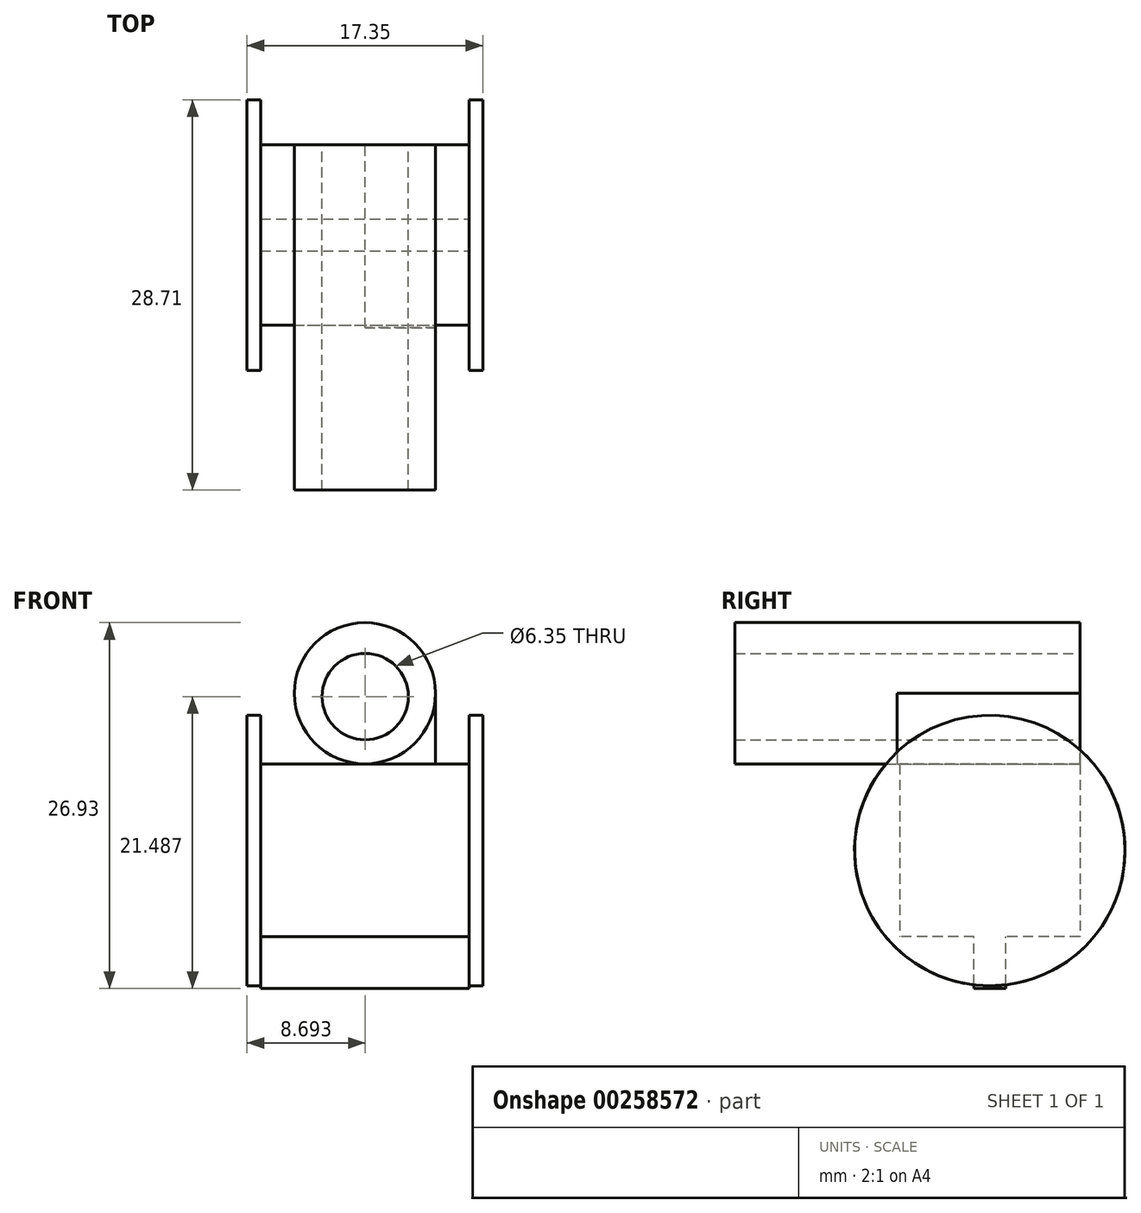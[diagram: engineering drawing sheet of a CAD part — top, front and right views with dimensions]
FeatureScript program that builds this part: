
annotation { "Feature Type Name" : "Feature", "Feature Type Description" : "" }
export const myFeature = defineFeature(function(context is Context, id is Id, definition is map)
    precondition{}
    {
        {
            var Q0;
            Q0=qCreatedBy(makeId("Top.planeOp"),FACE);
            var sketch = newSketch(context, id + "F0", { "sketchPlane" : qUnion([Q0])});
            skLineSegment(sketch, "E0.bottom", {"start": v(-55.18, 45.23) * mm, "end": v(-39.83, 45.23) * mm});
            skLineSegment(sketch, "E0.top", {"start": v(-55.18, 31.95) * mm, "end": v(-39.83, 31.95) * mm});
            skLineSegment(sketch, "E0.left", {"start": v(-55.18, 45.23) * mm, "end": v(-55.18, 31.95) * mm});
            skLineSegment(sketch, "E0.right", {"start": v(-39.83, 45.23) * mm, "end": v(-39.83, 31.95) * mm});
            skSolve(sketch);
        }
        {
            var Q0;
            Q0 = qSketchRegion(id + "F0", true);
            extrude(context, id + "F1", {"entities" : qUnion([Q0]), "depth" : 12.7 * mm});
        }
        {
            var Q0;
            Q0=makeQuery(id+"F1.opExtrude","SWEPT_FACE",FACE,{"disambiguationData":[OSD([sQuery(id+"F0.wireOp",EDGE,"E0.left")])]});
            var sketch = newSketch(context, id + "F2", { "sketchPlane" : qUnion([Q0])});
            skCircle(sketch, "E1", {"center": v(-38.59, 6.35) * mm, "radius": 9.95 * mm});
            skPoint(sketch, "E1.centerSnap0", {"position": v(-31.95, 6.35) * mm});
            skPoint(sketch, "E1.centerSnap1", {"position": v(-38.59, 12.7) * mm});
            skSolve(sketch);
        }
        {
            var Q0;
            Q0=makeQuery(id+"F1.opExtrude","SWEPT_FACE",FACE,{"disambiguationData":[OSD([sQuery(id+"F0.wireOp",EDGE,"E0.right")])]});
            var sketch = newSketch(context, id + "F3", { "sketchPlane" : qUnion([Q0])});
            skCircle(sketch, "E2", {"center": v(38.59, 6.35) * mm, "radius": 9.95 * mm});
            skPoint(sketch, "E2.centerSnap0", {"position": v(38.59, 12.7) * mm});
            skPoint(sketch, "E2.centerSnap1", {"position": v(31.95, 6.35) * mm});
            skSolve(sketch);
        }
        {
            var Q0;
            Q0=makeQuery(id+"F2.imprint","IMPRINT",FACE,{"disambiguationData":[TD([[makeQuery(id+"F2.imprint","IMPRINT",EDGE,{"derivedFrom":sQuery(id+"F2.wireOp",EDGE,"E1")}),1.0]])]});
            var Q1;
            {var subQ0=sQuery(id+"F0.wireOp",EDGE,"E0.left");Q1=makeQuery(id+"F2.imprint","IMPRINT",FACE,{"disambiguationData":[TD([[makeQuery(id+"F2.imprint","IMPRINT",EDGE,{"derivedFrom":makeQuery(id+"F1.opExtrude","CAP_EDGE",EDGE,{"disambiguationData":[OSD([subQ0])],"isStart":true})}),1.0]])]});}
            extrude(context, id + "F4", {"entities" : qUnion([Q0, Q1]), "operationType" : NewBodyOperationType.ADD, "depth" : 1 * mm});
        }
        {
            var Q0;
            Q0=makeQuery(id+"F3.imprint","IMPRINT",FACE,{"disambiguationData":[TD([[makeQuery(id+"F3.imprint","IMPRINT",EDGE,{"derivedFrom":sQuery(id+"F3.wireOp",EDGE,"E2")}),1.0]])]});
            var Q1;
            {var subQ0=sQuery(id+"F0.wireOp",EDGE,"E0.right");Q1=makeQuery(id+"F3.imprint","IMPRINT",FACE,{"disambiguationData":[TD([[makeQuery(id+"F3.imprint","IMPRINT",EDGE,{"derivedFrom":makeQuery(id+"F1.opExtrude","CAP_EDGE",EDGE,{"disambiguationData":[OSD([subQ0])],"isStart":true})}),-1.0]])]});}
            extrude(context, id + "F5", {"entities" : qUnion([Q0, Q1]), "operationType" : NewBodyOperationType.ADD, "depth" : 1 * mm});
        }
        {
            var Q0;
            Q0=makeQuery(id+"F1.opExtrude","SWEPT_FACE",FACE,{"disambiguationData":[OSD([sQuery(id+"F0.wireOp",EDGE,"E0.bottom")])]});
            var sketch = newSketch(context, id + "F6", { "sketchPlane" : qUnion([Q0])});
            skLineSegment(sketch, "E3", {"start": v(47.5, 12.7) * mm, "end": v(47.5, 17.92) * mm});
            skCircle(sketch, "E4", {"center": v(47.5, 17.92) * mm, "radius": 5.2 * mm});
            skLineSegment(sketch, "E5", {"start": v(52.7, 17.92) * mm, "end": v(52.7, 12.7) * mm});
            skLineSegment(sketch, "E6", {"start": v(52.7, 12.7) * mm, "end": v(52.7, 17.92) * mm});
            skLineSegment(sketch, "E7", {"start": v(42.31, 17.92) * mm, "end": v(42.31, 12.7) * mm});
            skSolve(sketch);
        }
        {
            var Q0;
            {var subQ5=sQuery(id+"F6.wireOp",EDGE,"E7");Q0=makeQuery(id+"F6.imprint","IMPRINT",FACE,{"disambiguationData":[TD([[makeQuery(id+"F6.imprint","IMPRINT",EDGE,{"derivedFrom":subQ5}),1.0]])]});}
            var Q1;
            {var subQ5=sQuery(id+"F6.wireOp",EDGE,"E6");Q1=makeQuery(id+"F6.imprint","IMPRINT",FACE,{"disambiguationData":[TD([[makeQuery(id+"F6.imprint","IMPRINT",EDGE,{"derivedFrom":subQ5}),1.0]])]});}
            extrude(context, id + "F7", {"entities" : qUnion([Q0, Q1]), "oppositeDirection" : true, "depth" : 13.46 * mm});
        }
        {
            var Q0;
            {var subQ0=sQuery(id+"F6.wireOp",EDGE,"E4");var subQ1=makeQuery(id+"F6.imprint","INTERSECT",VERTEX,{"derivedFrom":[subQ0,sQuery(id+"F6.wireOp",EDGE,"E6")]});Q0=makeQuery(id+"F6.imprint","IMPRINT",FACE,{"disambiguationData":[TD([[makeQuery(id+"F6.imprint","IMPRINT",EDGE,{"disambiguationData":[TD([[subQ1,-1.0]])],"derivedFrom":subQ0}),1.0]])]});}
            var Q1;
            {var subQ0=sQuery(id+"F0.wireOp",EDGE,"E0.bottom");Q1=makeQuery(id+"F6.imprint","IMPRINT",FACE,{"disambiguationData":[TD([[makeQuery(id+"F6.imprint","IMPRINT",EDGE,{"derivedFrom":makeQuery(id+"F1.opExtrude","CAP_EDGE",EDGE,{"disambiguationData":[OSD([subQ0])],"isStart":true})}),-1.0]])]});}
            extrude(context, id + "F8", {"entities" : qUnion([Q0, Q1]), "oppositeDirection" : true, "depth" : 25.4 * mm});
        }
        {
            var Q0;
            {var subQ0=sQuery(id+"F6.wireOp",EDGE,"E4");var subQ1=makeQuery(id+"F6.imprint","INTERSECT",VERTEX,{"derivedFrom":[subQ0,sQuery(id+"F6.wireOp",EDGE,"E6")]});Q0=makeQuery(id+"F6.imprint","IMPRINT",FACE,{"disambiguationData":[TD([[makeQuery(id+"F6.imprint","IMPRINT",EDGE,{"disambiguationData":[TD([[subQ1,-1.0]])],"derivedFrom":subQ0}),1.0]])]});}
            var sketch = newSketch(context, id + "F9", { "sketchPlane" : qUnion([Q0])});
            skCircle(sketch, "E8", {"center": v(47.49, 17.68) * mm, "radius": 2.26 * mm});
            skSolve(sketch);
        }
        {
            var Q0;
            Q0=makeQuery(id+"F8.opExtrude","SWEPT_BODY",BODY,{"disambiguationData":[OSD([sQuery(id+"F0.wireOp",EDGE,"E0.bottom"),sQuery(id+"F0.wireOp",EDGE,"E0.left"),sQuery(id+"F0.wireOp",EDGE,"E0.right")])]});
            deleteBodies(context, id + "F10", {"entities" : qUnion([Q0])});
        }
        {
            var Q0;
            Q0=sQuery(id+"F9.wireOp",VERTEX,"E8.center");
            var Q1;
            Q1=makeQuery(id+"F8.opExtrude","SWEPT_BODY",BODY,{"disambiguationData":[OSD([sQuery(id+"F6.wireOp",EDGE,"E4")])]});
            hole(context, id + "F11", {"style" : HoleStyle.SIMPLE, "endStyle" : HoleEndStyle.THROUGH, "holeDiameter" : 6.35 * mm, "tappedDepth" : 12.7 * mm, "tapClearance" : 3, "locations" : qUnion([Q0]), "scope" : qUnion([Q1])});
        }
        {
            var Q0;
            Q0=makeQuery(id+"F1.opExtrude","CAP_FACE",FACE,{"disambiguationData":[OSD([sQuery(id+"F0.wireOp",EDGE,"E0.bottom"),sQuery(id+"F0.wireOp",EDGE,"E0.top"),sQuery(id+"F0.wireOp",EDGE,"E0.left"),sQuery(id+"F0.wireOp",EDGE,"E0.right")])],"isStart":true});
            var sketch = newSketch(context, id + "F12", { "sketchPlane" : qUnion([Q0])});
            skLineSegment(sketch, "E9.bottom", {"start": v(-55.18, -37.42) * mm, "end": v(-39.83, -37.42) * mm});
            skLineSegment(sketch, "E9.top", {"start": v(-55.18, -39.77) * mm, "end": v(-39.83, -39.77) * mm});
            skLineSegment(sketch, "E9.left", {"start": v(-55.18, -37.42) * mm, "end": v(-55.18, -39.77) * mm});
            skLineSegment(sketch, "E9.right", {"start": v(-39.83, -37.42) * mm, "end": v(-39.83, -39.77) * mm});
            skSolve(sketch);
        }
        {
            var Q0;
            Q0 = qSketchRegion(id + "F12", true);
            extrude(context, id + "F13", {"entities" : qUnion([Q0]), "operationType" : NewBodyOperationType.ADD, "depth" : 3.8 * mm});
        }
    });
